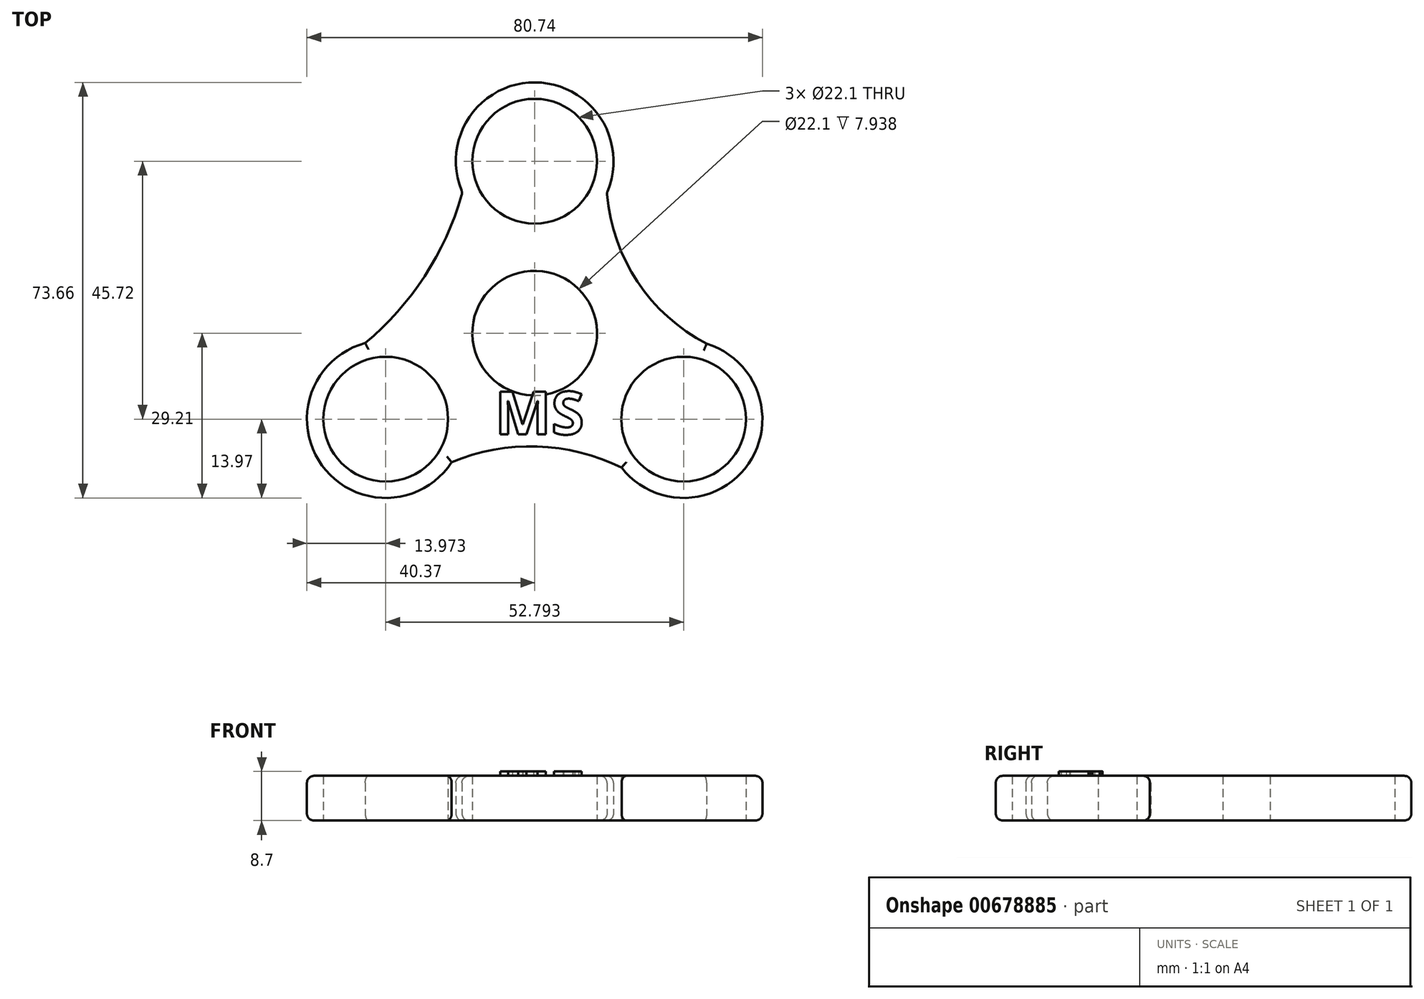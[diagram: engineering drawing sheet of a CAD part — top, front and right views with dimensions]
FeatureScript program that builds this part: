
annotation { "Feature Type Name" : "Feature", "Feature Type Description" : "" }
export const myFeature = defineFeature(function(context is Context, id is Id, definition is map)
    precondition{}
    {
        {
            var Q0;
            Q0=qCreatedBy(makeId("Top.planeOp"),FACE);
            var sketch = newSketch(context, id + "F0", { "sketchPlane" : qUnion([Q0])});
            skCircle(sketch, "E0", {"center": v(0, 0) * mm, "radius": 44.45 * mm});
            skCircle(sketch, "E1", {"center": v(0, 0) * mm, "radius": 11.05 * mm});
            skLineSegment(sketch, "E2", {"start": v(0, 0) * mm, "end": v(0, 30.48) * mm});
            skCircle(sketch, "E3", {"center": v(0, 30.48) * mm, "radius": 11.05 * mm});
            skCircle(sketch, "E4.1.0", {"center": v(-26.4, -15.24) * mm, "radius": 11.05 * mm});
            skCircle(sketch, "E4.2.0", {"center": v(26.4, -15.24) * mm, "radius": 11.05 * mm});
            skArc(sketch, "E5", {"start": v(-30.04, -1.75) * mm, "mid": v(-37.7, -23.44) * mm, "end": v(-14.7, -22.9) * mm});
            skArc(sketch, "E6", {"start": v(15.4, -23.86) * mm, "mid": v(37.92, -23.14) * mm, "end": v(30.48, -1.88) * mm});
            skArc(sketch, "E7", {"start": v(12.81, 24.92) * mm, "mid": v(0, 44.45) * mm, "end": v(-12.81, 24.92) * mm});
            skArc(sketch, "E8", {"start": v(15.4, -23.86) * mm, "mid": v(0.45, -20.1) * mm, "end": v(-14.7, -22.9) * mm});
            skArc(sketch, "E9", {"start": v(12.81, 24.92) * mm, "mid": v(18.16, 9.22) * mm, "end": v(30.48, -1.88) * mm});
            skArc(sketch, "E10", {"start": v(-30.04, -1.75) * mm, "mid": v(-19.39, 10.26) * mm, "end": v(-12.81, 24.92) * mm});
            skSolve(sketch);
        }
        {
            var Q0;
            Q0=makeQuery(id+"F0.imprint","IMPRINT",FACE,{"disambiguationData":[TD([[makeQuery(id+"F0.imprint","IMPRINT",EDGE,{"derivedFrom":sQuery(id+"F0.wireOp",EDGE,"E1")}),-1.0]])]});
            extrude(context, id + "F1", {"entities" : qUnion([Q0]), "depth" : 7.94 * mm, "offsetDistance" : 25.4 * mm});
        }
        {
            var Q0;
            Q0=makeQuery(id+"F1.opExtrude","CAP_EDGE",EDGE,{"disambiguationData":[OSD([sQuery(id+"F0.wireOp",EDGE,"E5")])],"isStart":false});
            var Q1;
            Q1=makeQuery(id+"F1.opExtrude","CAP_EDGE",EDGE,{"disambiguationData":[OSD([sQuery(id+"F0.wireOp",EDGE,"E8")])],"isStart":false});
            var Q2;
            Q2=makeQuery(id+"F1.opExtrude","CAP_EDGE",EDGE,{"disambiguationData":[OSD([sQuery(id+"F0.wireOp",EDGE,"E6")])],"isStart":false});
            var Q3;
            Q3=makeQuery(id+"F1.opExtrude","CAP_EDGE",EDGE,{"disambiguationData":[OSD([sQuery(id+"F0.wireOp",EDGE,"E9")])],"isStart":false});
            var Q4;
            Q4=makeQuery(id+"F1.opExtrude","CAP_EDGE",EDGE,{"disambiguationData":[OSD([sQuery(id+"F0.wireOp",EDGE,"E7")])],"isStart":false});
            var Q5;
            Q5=makeQuery(id+"F1.opExtrude","CAP_EDGE",EDGE,{"disambiguationData":[OSD([sQuery(id+"F0.wireOp",EDGE,"E10")])],"isStart":false});
            var Q6;
            Q6=makeQuery(id+"F1.opExtrude","CAP_EDGE",EDGE,{"disambiguationData":[OSD([sQuery(id+"F0.wireOp",EDGE,"E9")])],"isStart":true});
            var Q7;
            Q7=makeQuery(id+"F1.opExtrude","CAP_EDGE",EDGE,{"disambiguationData":[OSD([sQuery(id+"F0.wireOp",EDGE,"E7")])],"isStart":true});
            var Q8;
            Q8=makeQuery(id+"F1.opExtrude","SWEPT_EDGE",EDGE,{"disambiguationData":[OSD([sQuery(id+"F0.wireOp",EDGE,"E7"),sQuery(id+"F0.wireOp",EDGE,"E10")])]});
            var Q9;
            Q9=makeQuery(id+"F1.opExtrude","SWEPT_EDGE",EDGE,{"disambiguationData":[OSD([sQuery(id+"F0.wireOp",EDGE,"E7"),sQuery(id+"F0.wireOp",EDGE,"E9")])]});
            var Q10;
            Q10=makeQuery(id+"F1.opExtrude","CAP_EDGE",EDGE,{"disambiguationData":[OSD([sQuery(id+"F0.wireOp",EDGE,"E8")])],"isStart":true});
            var Q11;
            Q11=makeQuery(id+"F1.opExtrude","CAP_EDGE",EDGE,{"disambiguationData":[OSD([sQuery(id+"F0.wireOp",EDGE,"E6")])],"isStart":true});
            var Q12;
            Q12=makeQuery(id+"F1.opExtrude","CAP_EDGE",EDGE,{"disambiguationData":[OSD([sQuery(id+"F0.wireOp",EDGE,"E10")])],"isStart":true});
            var Q13;
            Q13=makeQuery(id+"F1.opExtrude","CAP_EDGE",EDGE,{"disambiguationData":[OSD([sQuery(id+"F0.wireOp",EDGE,"E5")])],"isStart":true});
            fillet(context, id + "F2", {"entities" : qUnion([Q0, Q1, Q2, Q3, Q4, Q5, Q6, Q7, Q8, Q9, Q10, Q11, Q12, Q13]), "radius" : 1.27 * mm, "tangentPropagation" : true, "allowEdgeOverflow" : false});
        }
        {
            var Q0;
            Q0=makeQuery(id+"F1.opExtrude","CAP_FACE",FACE,{"disambiguationData":[OSD([sQuery(id+"F0.wireOp",EDGE,"E1"),sQuery(id+"F0.wireOp",EDGE,"E3"),sQuery(id+"F0.wireOp",EDGE,"E4.1.0"),sQuery(id+"F0.wireOp",EDGE,"E4.2.0"),sQuery(id+"F0.wireOp",EDGE,"E5"),sQuery(id+"F0.wireOp",EDGE,"E6"),sQuery(id+"F0.wireOp",EDGE,"E7"),sQuery(id+"F0.wireOp",EDGE,"E8"),sQuery(id+"F0.wireOp",EDGE,"E9"),sQuery(id+"F0.wireOp",EDGE,"E10")])],"isStart":false});
            var sketch = newSketch(context, id + "F3", { "sketchPlane" : qUnion([Q0])});
            skText(sketch, "E11", { "text": "MS", "fontName": "OpenSans-Bold.ttf"});
            const initialGuessF3  = {"E11": [-0.00705, -0.01794, 1, 0, 0.00762]};
            skSetInitialGuess(sketch, initialGuessF3);
            skSolve(sketch);
        }
        {
            var Q0;
            Q0 = qSketchRegion(id + "F3", true);
            extrude(context, id + "F4", {"entities" : qUnion([Q0]), "operationType" : NewBodyOperationType.ADD, "depth" : 0.76 * mm, "offsetDistance" : 25.4 * mm});
        }
    });
